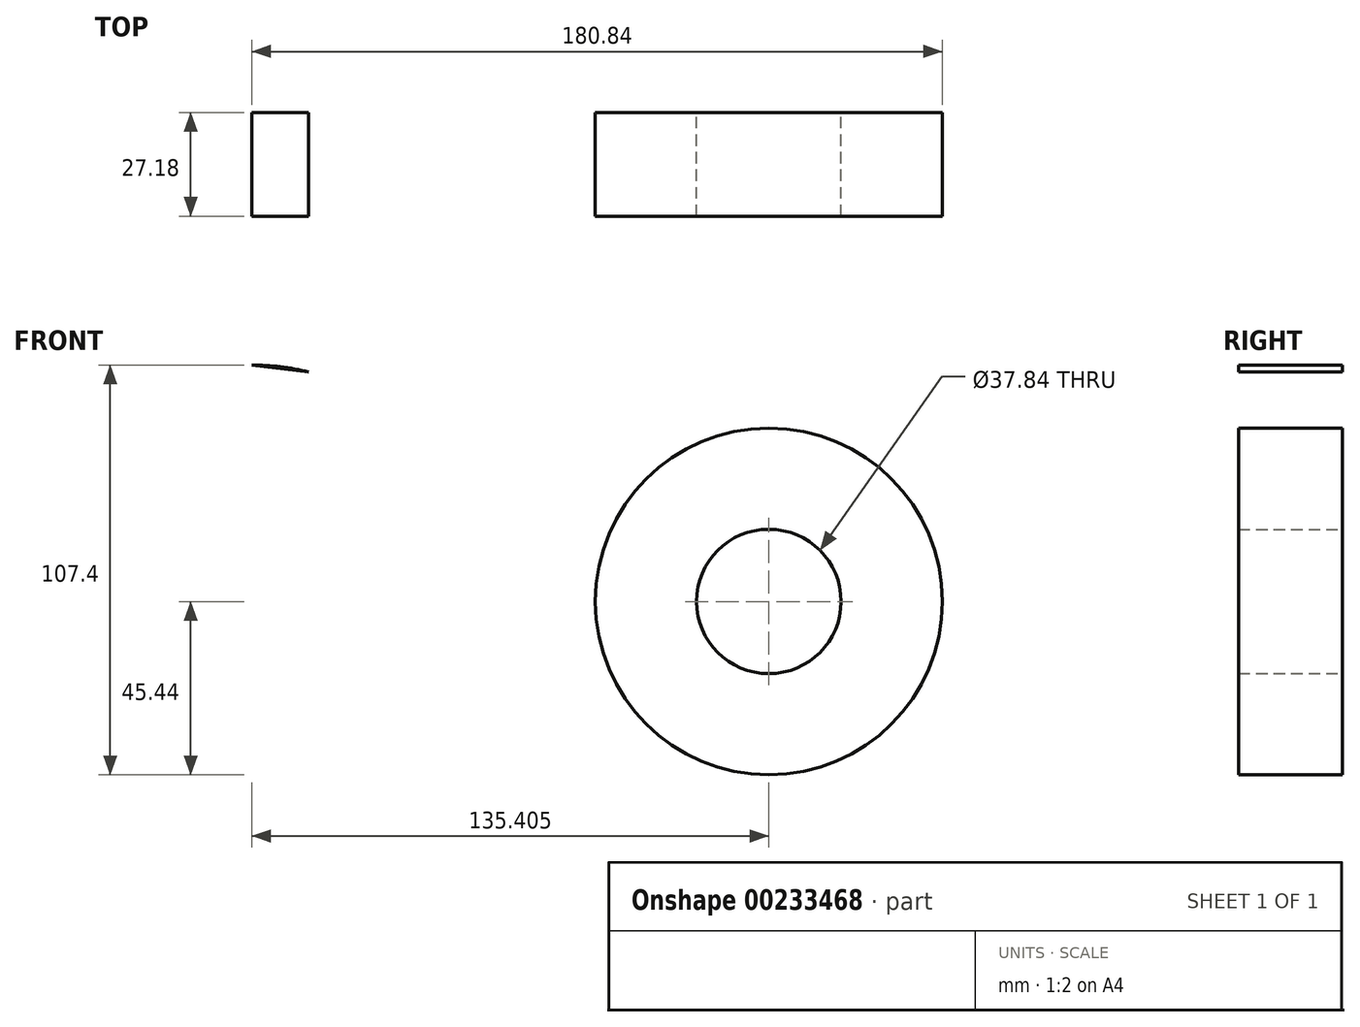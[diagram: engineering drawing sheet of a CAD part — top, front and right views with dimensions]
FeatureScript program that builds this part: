
annotation { "Feature Type Name" : "Feature", "Feature Type Description" : "" }
export const myFeature = defineFeature(function(context is Context, id is Id, definition is map)
    precondition{}
    {
        {
            var Q0;
            Q0=qCreatedBy(makeId("Front.planeOp"),FACE);
            var sketch = newSketch(context, id + "F0", { "sketchPlane" : qUnion([Q0])});
            skCircle(sketch, "E0", {"center": v(0, 0) * mm, "radius": 61.96 * mm});
            skCircle(sketch, "E1", {"center": v(135.4, 0) * mm, "radius": 45.44 * mm});
            skLineSegment(sketch, "E2", {"start": v(0, 61.96) * mm, "end": v(135.44, 45.44) * mm});
            skLineSegment(sketch, "E3", {"start": v(0, -61.96) * mm, "end": v(134.68, -45.43) * mm});
            skArc(sketch, "E4", {"start": v(-16.2, -7.15) * mm, "mid": v(0, -17.7) * mm, "end": v(16.2, -7.15) * mm});
            skLineSegment(sketch, "E5.bottom", {"start": v(26.93, 7.15) * mm, "end": v(16.2, 7.15) * mm});
            skLineSegment(sketch, "E5.top", {"start": v(26.93, -7.15) * mm, "end": v(16.2, -7.15) * mm});
            skLineSegment(sketch, "E5.left", {"start": v(26.93, 7.15) * mm, "end": v(26.93, -7.15) * mm});
            skLineSegment(sketch, "E5.right", {"start": v(-26.93, 7.15) * mm, "end": v(-26.93, -7.15) * mm});
            skLineSegment(sketch, "E6.trimOffspring", {"start": v(-16.2, 7.15) * mm, "end": v(-26.93, 7.15) * mm});
            skLineSegment(sketch, "E7.trimOffspring", {"start": v(-16.2, -7.15) * mm, "end": v(-26.93, -7.15) * mm});
            skArc(sketch, "E8.trimOffspring", {"start": v(16.2, 7.15) * mm, "mid": v(0, 17.7) * mm, "end": v(-16.2, 7.15) * mm});
            skCircle(sketch, "E9", {"center": v(135.4, 0) * mm, "radius": 18.92 * mm});
            skSolve(sketch);
        }
        {
            var Q0;
            {var subQ0=sQuery(id+"F0.wireOp",EDGE,"E2");var subQ1=sQuery(id+"F0.wireOp",EDGE,"E0");var subQ2=makeQuery(id+"F0.imprint","INTERSECT",VERTEX,{"disambiguationData":[OD(0.0)],"derivedFrom":[subQ1,subQ0]});Q0=makeQuery(id+"F0.imprint","IMPRINT",FACE,{"disambiguationData":[TD([[makeQuery(id+"F0.imprint","IMPRINT",EDGE,{"disambiguationData":[TD([[subQ2,-1.0]])],"derivedFrom":subQ1}),1.0]])]});}
            var Q1;
            {var subQ0=sQuery(id+"F0.wireOp",EDGE,"E2");var subQ1=sQuery(id+"F0.wireOp",EDGE,"E0");var subQ2=makeQuery(id+"F0.imprint","INTERSECT",VERTEX,{"disambiguationData":[OD(1.0)],"derivedFrom":[subQ1,subQ0]});Q1=makeQuery(id+"F0.imprint","IMPRINT",FACE,{"disambiguationData":[TD([[makeQuery(id+"F0.imprint","IMPRINT",EDGE,{"disambiguationData":[TD([[subQ2,1.0]])],"derivedFrom":subQ1}),-1.0]])]});}
            var Q2;
            {var subQ0=sQuery(id+"F0.wireOp",EDGE,"E1");var subQ1=makeQuery(id+"F0.imprint","INTERSECT",VERTEX,{"derivedFrom":[subQ0,sQuery(id+"F0.wireOp",EDGE,"E2")]});Q2=makeQuery(id+"F0.imprint","IMPRINT",FACE,{"disambiguationData":[TD([[makeQuery(id+"F0.imprint","IMPRINT",EDGE,{"disambiguationData":[TD([[subQ1,-1.0]])],"derivedFrom":subQ0}),1.0]])]});}
            extrude(context, id + "F1", {"entities" : qUnion([Q0, Q1, Q2]), "depth" : 27.18 * mm});
        }
    });
